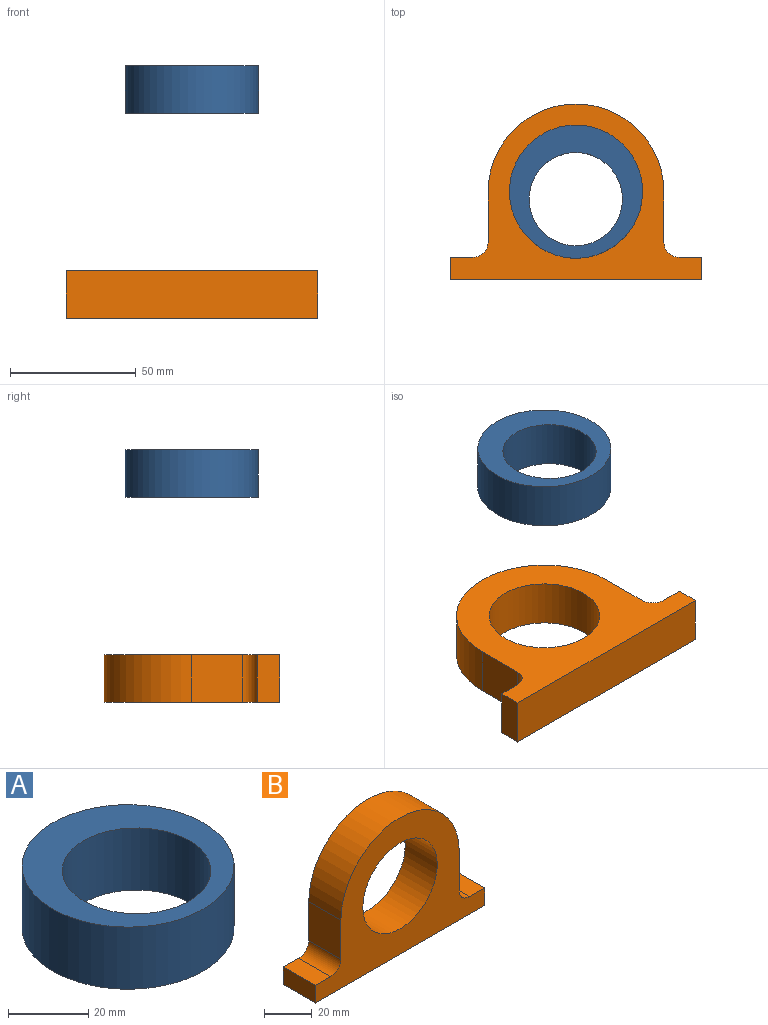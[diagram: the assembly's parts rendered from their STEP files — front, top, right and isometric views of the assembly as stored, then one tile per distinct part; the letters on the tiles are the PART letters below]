
ASSEMBLY  parts=2 mates=1
PART A: 4 faces, bbox 53x53x19 mm
  f0: cylinder r=26.5mm len=53mm, axis (0,0,-1), area 3163.6mm2, adj f1,f2
  f1: plane 53x53mm, normal (0,0,1), area 1124.6mm2, adj f0,f3
  f2: plane 53x53mm, normal (0,0,-1), area 1124.6mm2, adj f0,f3
  f3: cylinder r=18.55mm len=37.11mm, axis (0,0,1), area 2215.1mm2, adj f1,f2
PART B: 13 faces, bbox 100x19x70 mm
  f0: plane 19x9mm, normal (0,0,1), area 171mm2, adj f7,f9,f10,f11
  f1: plane 20x19mm, normal (1,0,0), area 380mm2, adj f2,f9,f10,f11
  f2: cylinder r=35mm len=70mm, axis (0,1,0), area 2089.2mm2, adj f1,f3,f9,f10
  f3: plane 20x19mm, normal (-1,0,0), area 380mm2, adj f2,f9,f10,f12
  f4: plane 19x9mm, normal (0,0,1), area 171mm2, adj f5,f9,f10,f12
  f5: plane 19x9mm, normal (-1,0,0), area 171mm2, adj f4,f6,f9,f10
  f6: plane 100x19mm, normal (0,0,-1), area 1900mm2, adj f5,f7,f9,f10
  f7: plane 19x9mm, normal (1,0,0), area 171mm2, adj f0,f6,f9,f10
  f8: cylinder r=22mm len=44mm, axis (0,1,0), area 2626.4mm2, adj f9,f10
  f9: plane 100x70mm, normal (0,-1,0), area 3139.1mm2, adj f0,f1,f2,f3,f4,f5,f6,f7
  f10: plane 100x70mm, normal (0,1,0), area 3139.1mm2, adj f0,f1,f2,f3,f4,f5,f6,f7
  f11: cylinder r=6mm len=19mm, axis (0,-1,0), area 179.1mm2, adj f0,f1,f9,f10
  f12: cylinder r=6mm len=19mm, axis (0,-1,0), area 179.1mm2, adj f3,f4,f9,f10
PLACE A rot(axis=(0,0,-1),1.9deg) t=(-24.27,38.05,10.81)mm
PLACE B rot(axis=(-1,0,0),90deg) t=(-24.27,38.05,-70.79)mm fixed
MATE cylindrical B.f8 <-> A.f0  axis (0,0,-1) through (-24.27,38.05,-61.29)mm
